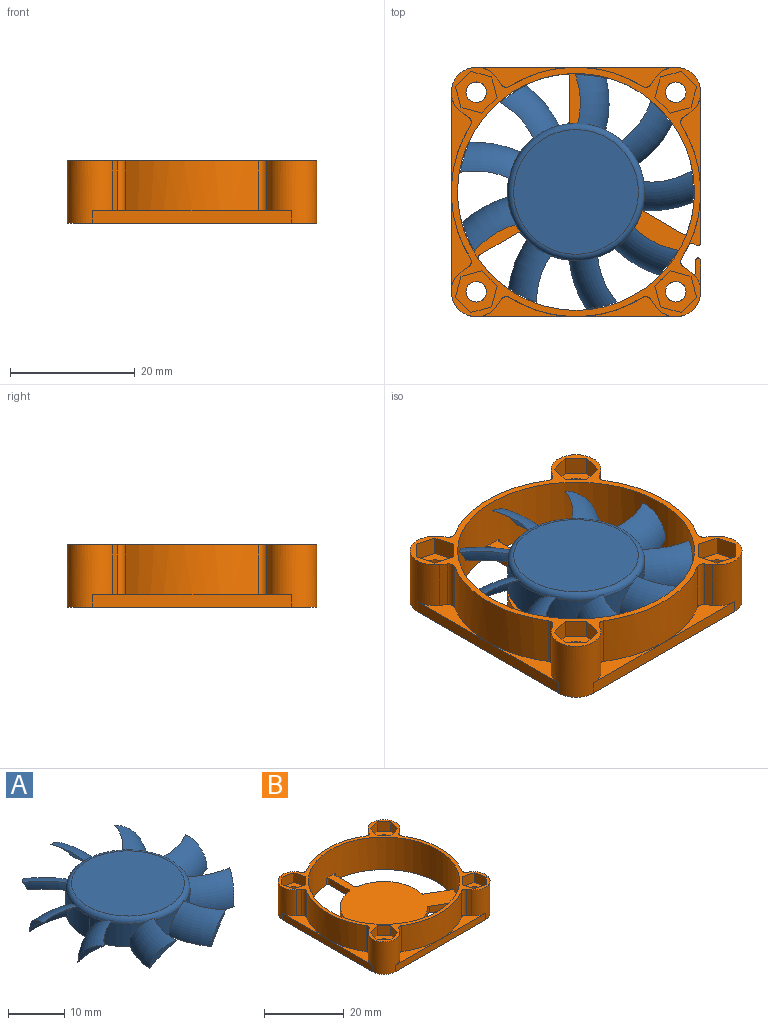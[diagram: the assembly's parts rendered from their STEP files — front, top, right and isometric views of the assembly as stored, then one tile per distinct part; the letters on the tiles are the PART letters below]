
ASSEMBLY  parts=2 mates=1
PART A: 32 faces, bbox 42.3x42.5x6 mm
  f0: cylinder r=11mm len=22mm, axis (0,0,-1), area 307.6mm2, adj f1,f3,f4,f5,f6,f8,f9,f11
  f1: cylinder r=11mm len=4.52mm, axis (0,0,-1), area 3.9mm2, adj f0,f4,f12
  f2: plane 20x20mm, normal (0,0,1), area 314.2mm2, adj f4
  f3: plane 22x22mm, normal (0,0,-1), area 380.1mm2, adj f0
  f4: torus R=10mm, axis (0,0,1), area 102.2mm2, adj f0,f1,f2,f5,f6,f8,f9,f11
  f5: torus R=5.4mm, axis (0,0,-1), area 55.4mm2, adj f0,f4,f6,f7
  f6: torus R=12.73mm, axis (0,0,-1), area 60.2mm2, adj f0,f4,f5,f7
  f7: cylinder r=18.8mm len=4.97mm, axis (0,0,1), area 4.5mm2, adj f5,f6
  f8: torus R=5.4mm, axis (0,0,-1), area 55.4mm2, adj f0,f4,f9,f10
  f9: torus R=12.73mm, axis (0,0,-1), area 60.2mm2, adj f0,f4,f8,f10
  f10: cylinder r=18.8mm len=4.97mm, axis (0,0,1), area 4.5mm2, adj f8,f9
  f11: torus R=5.4mm, axis (0,0,-1), area 55.4mm2, adj f0,f4,f12,f13
  f12: torus R=12.73mm, axis (0,0,-1), area 60.2mm2, adj f1,f4,f11,f13
  f13: cylinder r=18.8mm len=4.97mm, axis (0,0,1), area 4.5mm2, adj f11,f12
  f14: torus R=5.4mm, axis (0,0,-1), area 55.4mm2, adj f0,f4,f15,f16
  f15: torus R=12.73mm, axis (0,0,-1), area 60.2mm2, adj f0,f4,f14,f16
  f16: cylinder r=18.8mm len=4.97mm, axis (0,0,1), area 4.5mm2, adj f14,f15
  f17: torus R=5.4mm, axis (0,0,-1), area 55.4mm2, adj f0,f4,f18,f19
  f18: torus R=12.73mm, axis (0,0,-1), area 60.2mm2, adj f0,f4,f17,f19
  f19: cylinder r=18.8mm len=4.97mm, axis (0,0,1), area 4.5mm2, adj f17,f18
  f20: torus R=5.4mm, axis (0,0,-1), area 55.4mm2, adj f0,f4,f21,f22
  f21: torus R=12.73mm, axis (0,0,-1), area 60.2mm2, adj f0,f4,f20,f22
  f22: cylinder r=18.8mm len=4.99mm, axis (0,0,1), area 4.5mm2, adj f20,f21
  f23: torus R=5.4mm, axis (0,0,-1), area 55.4mm2, adj f0,f4,f24,f25
  f24: torus R=12.73mm, axis (0,0,-1), area 60.2mm2, adj f0,f4,f23,f25
  f25: cylinder r=18.8mm len=4.97mm, axis (0,0,1), area 4.5mm2, adj f23,f24
  f26: torus R=5.4mm, axis (0,0,-1), area 55.4mm2, adj f0,f4,f27,f28
  f27: torus R=12.73mm, axis (0,0,-1), area 60.2mm2, adj f0,f4,f26,f28
  f28: cylinder r=18.8mm len=5mm, axis (0,0,1), area 4.5mm2, adj f26,f27
  f29: torus R=5.4mm, axis (0,0,-1), area 55.4mm2, adj f0,f4,f30,f31
  f30: torus R=12.73mm, axis (0,0,-1), area 60.2mm2, adj f0,f4,f29,f31
  f31: cylinder r=18.8mm len=4.97mm, axis (0,0,1), area 4.5mm2, adj f29,f30
PART B: 115 faces, bbox 40x40x10 mm
  f0: plane 10.28x5.94mm, normal (0.5,0.87,0), area 11.9mm2, adj f19,f33,f35,f80,f81,f82
  f1: plane 2x1.78mm, normal (-1,0,0), area 3.6mm2, adj f8,f33,f81,f97
  f2: plane 16x3.21mm, normal (0,0,1), area 18mm2, adj f26,f27,f56,f57,f100
  f3: plane 16x3.21mm, normal (0,0,1), area 18mm2, adj f25,f26,f65,f69,f106
  f4: plane 16x3.21mm, normal (0,0,1), area 18mm2, adj f21,f22,f34,f60,f102
  f5: plane 16x3.21mm, normal (0,0,1), area 18mm2, adj f23,f24,f62,f63,f104
  f6: plane 16x3.21mm, normal (0,0,1), area 18mm2, adj f27,f28,f57,f58,f101
  f7: plane 35.04x31.24mm, normal (0,0,1), area 457.1mm2, adj f12,f13,f14,f15,f16,f17,f18,f30
  f8: plane 5.45x1.07mm, normal (0,0,1), area 3mm2, adj f1,f28,f29,f81,f96,f97
  f9: plane 16x3.21mm, normal (0,0,1), area 18mm2, adj f22,f23,f61,f62,f103
  f10: plane 8.58x1.89mm, normal (0,0,1), area 5.1mm2, adj f20,f21,f34,f76,f89
  f11: plane 16x3.21mm, normal (0,0,1), area 18mm2, adj f24,f25,f64,f65,f105
  f12: plane 7.04x2mm, normal (1,0,0), area 14.1mm2, adj f7,f33,f87,f92
  f13: cylinder r=19mm len=38mm, axis (0,0,1), area 1168mm2, adj f7,f33,f71,f83,f84,f85,f86,f87
  f14: plane 6.22x3.59mm, normal (0.5,0.87,0), area 14.4mm2, adj f7,f33,f88,f95
  f15: plane 6.09x3.52mm, normal (0.5,-0.87,0), area 14.1mm2, adj f7,f33,f84,f90
  f16: cylinder r=11mm len=16.31mm, axis (0,0,1), area 36.9mm2, adj f7,f33,f90,f94
  f17: plane 6.09x3.52mm, normal (-0.5,0.87,0), area 14.1mm2, adj f7,f33,f85,f91
  f18: plane 7.04x2mm, normal (-1,0,0), area 14.1mm2, adj f7,f33,f86,f93
  f19: cylinder r=11mm len=3.9mm, axis (0,0,1), area 4.4mm2, adj f0,f20,f33,f35,f77
  f20: plane 8.8x5.08mm, normal (-0.5,-0.87,0), area 6.1mm2, adj f10,f19,f33,f76,f77,f78,f89
  f21: plane 24.08x2mm, normal (1,0,0), area 48.2mm2, adj f4,f10,f22,f33,f89
  f22: cylinder r=4mm len=10mm, axis (0,0,1), area 124.5mm2, adj f4,f9,f21,f23,f33,f60,f61,f71
  f23: plane 32x2mm, normal (0,1,0), area 64mm2, adj f5,f9,f22,f24,f33
  f24: cylinder r=4mm len=10mm, axis (0,0,1), area 124.5mm2, adj f5,f11,f23,f25,f33,f63,f64,f71
  f25: plane 32x2mm, normal (-1,0,0), area 64mm2, adj f3,f11,f24,f26,f33
  f26: cylinder r=4mm len=10mm, axis (0,0,1), area 124.5mm2, adj f2,f3,f25,f27,f33,f56,f69,f71
  f27: plane 32x2mm, normal (0,-1,0), area 64mm2, adj f2,f6,f26,f28,f33
  f28: cylinder r=4mm len=10mm, axis (0,0,1), area 124.9mm2, adj f6,f8,f27,f29,f33,f58,f59,f71
  f29: plane 4.96x2mm, normal (1,0,0), area 9.9mm2, adj f8,f28,f33,f96
  f30: plane 6.22x3.59mm, normal (-0.5,-0.87,0), area 14.4mm2, adj f7,f33,f83,f94
  f31: cylinder r=11mm len=15.12mm, axis (0,0,1), area 40.3mm2, adj f7,f33,f91,f93
  f32: cylinder r=11mm len=13.49mm, axis (0,0,1), area 36.9mm2, adj f7,f33,f92,f95
  f33: plane 40x40mm, normal (0,0,-1), area 793.4mm2, adj f0,f1,f12,f13,f14,f15,f16,f17
  f34: cylinder r=20mm len=21.25mm, axis (0,0,1), area 180.4mm2, adj f4,f10,f71,f76,f79,f98,f102
  f35: plane 9.49x8.4mm, normal (0,0,-1), area 34.2mm2, adj f0,f19,f77,f79,f80
  f36: plane 3.35x3mm, normal (-0.26,-0.97,0), area 10.4mm2, adj f37,f70,f71,f75
  f37: plane 3.35x3mm, normal (-0.97,-0.26,0), area 10.4mm2, adj f36,f38,f71,f75
  f38: plane 3x2.45mm, normal (-0.71,0.71,0), area 10.4mm2, adj f37,f39,f71,f75
  f39: plane 3.35x3mm, normal (0.26,0.97,0), area 10.4mm2, adj f38,f40,f71,f75
  f40: plane 3.35x3mm, normal (0.97,0.26,0), area 10.4mm2, adj f39,f70,f71,f75
  f41: plane 3x2.45mm, normal (-0.71,0.71,0), area 10.4mm2, adj f42,f66,f71,f73
  f42: plane 3.35x3mm, normal (0.26,0.97,0), area 10.4mm2, adj f41,f43,f71,f73
  f43: plane 3.35x3mm, normal (0.97,0.26,0), area 10.4mm2, adj f42,f44,f71,f73
  f44: plane 3x2.45mm, normal (0.71,-0.71,0), area 10.4mm2, adj f43,f45,f71,f73
  f45: plane 3.35x3mm, normal (-0.26,-0.97,0), area 10.4mm2, adj f44,f66,f71,f73
  f46: plane 3.35x3mm, normal (-0.97,0.26,0), area 10.4mm2, adj f47,f67,f71,f72
  f47: plane 3.35x3mm, normal (-0.26,0.97,0), area 10.4mm2, adj f46,f48,f71,f72
  f48: plane 3x2.45mm, normal (0.71,0.71,0), area 10.4mm2, adj f47,f49,f71,f72
  f49: plane 3.35x3mm, normal (0.97,-0.26,0), area 10.4mm2, adj f48,f50,f71,f72
  f50: plane 3.35x3mm, normal (0.26,-0.97,0), area 10.4mm2, adj f49,f67,f71,f72
  f51: plane 3x2.45mm, normal (-0.71,-0.71,0), area 10.4mm2, adj f52,f68,f71,f74
  f52: plane 3.35x3mm, normal (-0.97,0.26,0), area 10.4mm2, adj f51,f53,f71,f74
  f53: plane 3.35x3mm, normal (-0.26,0.97,0), area 10.4mm2, adj f52,f54,f71,f74
  f54: plane 3x2.45mm, normal (0.71,0.71,0), area 10.4mm2, adj f53,f55,f71,f74
  f55: plane 3.35x3mm, normal (0.97,-0.26,0), area 10.4mm2, adj f54,f68,f71,f74
  f56: plane 8x1.06mm, normal (0.82,-0.57,0), area 10.4mm2, adj f2,f26,f71,f100
  f57: cylinder r=20mm len=21.25mm, axis (0,0,-1), area 179.2mm2, adj f2,f6,f71,f100,f101
  f58: plane 8x1.06mm, normal (-0.82,-0.57,0), area 10.4mm2, adj f6,f28,f71,f101
  f59: plane 8.5x1.06mm, normal (0.57,0.82,0), area 11mm2, adj f28,f71,f80,f98
  f60: plane 8x1.06mm, normal (0.57,-0.82,0), area 10.4mm2, adj f4,f22,f71,f102
  f61: plane 8x1.06mm, normal (-0.82,0.57,0), area 10.4mm2, adj f9,f22,f71,f103
  f62: cylinder r=20mm len=21.25mm, axis (0,0,-1), area 179.2mm2, adj f5,f9,f71,f103,f104
  f63: plane 8x1.06mm, normal (0.82,0.57,0), area 10.4mm2, adj f5,f24,f71,f104
  f64: plane 8x1.06mm, normal (-0.57,-0.82,0), area 10.4mm2, adj f11,f24,f71,f105
  f65: cylinder r=20mm len=21.25mm, axis (0,0,-1), area 179.2mm2, adj f3,f11,f71,f105,f106
  f66: plane 3.35x3mm, normal (-0.97,-0.26,0), area 10.4mm2, adj f41,f45,f71,f73
  f67: plane 3x2.45mm, normal (-0.71,-0.71,0), area 10.4mm2, adj f46,f50,f71,f72
  f68: plane 3.35x3mm, normal (0.26,-0.97,0), area 10.4mm2, adj f51,f55,f71,f74
  f69: plane 8x1.06mm, normal (-0.57,0.82,0), area 10.4mm2, adj f3,f26,f71,f106
  f70: plane 3x2.45mm, normal (0.71,-0.71,0), area 10.4mm2, adj f36,f40,f71,f75
  f71: plane 40x40mm, normal (0,0,1), area 183.3mm2, adj f13,f22,f24,f26,f28,f34,f36,f37
  f72: plane 6.69x6.69mm, normal (0,0,1), area 22.6mm2, adj f46,f47,f48,f49,f50,f67,f111
  f73: plane 6.69x6.69mm, normal (0,0,1), area 22.6mm2, adj f41,f42,f43,f44,f45,f66,f109
  f74: plane 6.69x6.69mm, normal (0,0,1), area 22.6mm2, adj f51,f52,f53,f54,f55,f68,f107
  f75: plane 6.69x6.69mm, normal (0,0,1), area 22.6mm2, adj f36,f37,f38,f39,f40,f70,f113
  f76: cylinder r=0.5mm len=0.7mm, axis (0,0,1), area 0.4mm2, adj f10,f20,f34,f78
  f77: cylinder r=0.5mm len=7.74mm, axis (0.87,-0.5,0), area 6.8mm2, adj f19,f20,f35,f78
  f78: bspline ~1.22x1.19mm, area 0.9mm2, adj f20,f76,f77,f79
  f79: torus R=19.5mm, axis (0,0,1), area 2.5mm2, adj f34,f35,f78,f99
  f80: cylinder r=0.5mm len=2.57mm, axis (0.82,-0.57,0), area 1.5mm2, adj f0,f35,f59,f82,f99
  f81: cylinder r=0.5mm len=2mm, axis (0,0,-1), area 1.7mm2, adj f0,f1,f8,f28,f33,f82
  f82: torus R=3.5mm, axis (0,0,1), area 0.4mm2, adj f0,f28,f80,f81
  f83: cylinder r=0.5mm len=2mm, axis (0,0,1), area 1.7mm2, adj f7,f13,f30,f33
  f84: cylinder r=0.5mm len=2mm, axis (0,0,1), area 1.7mm2, adj f7,f13,f15,f33
  f85: cylinder r=0.5mm len=2mm, axis (0,0,1), area 1.7mm2, adj f7,f13,f17,f33
  f86: cylinder r=0.5mm len=2mm, axis (0,0,1), area 1.7mm2, adj f7,f13,f18,f33
  f87: cylinder r=0.5mm len=2mm, axis (0,0,1), area 1.7mm2, adj f7,f12,f13,f33
  f88: cylinder r=0.5mm len=2mm, axis (0,0,1), area 1.7mm2, adj f7,f13,f14,f33
  f89: cylinder r=0.5mm len=2mm, axis (0,0,-1), area 2.1mm2, adj f10,f20,f21,f33
  f90: cylinder r=0.5mm len=2mm, axis (0,0,1), area 1.4mm2, adj f7,f15,f16,f33
  f91: cylinder r=0.5mm len=2mm, axis (0,0,1), area 1.4mm2, adj f7,f17,f31,f33
  f92: cylinder r=0.5mm len=2mm, axis (0,0,1), area 1.4mm2, adj f7,f12,f32,f33
  f93: cylinder r=0.5mm len=2mm, axis (0,0,1), area 1.4mm2, adj f7,f18,f31,f33
  f94: cylinder r=0.5mm len=2mm, axis (0,0,1), area 1.3mm2, adj f7,f16,f30,f33
  f95: cylinder r=0.5mm len=2mm, axis (0,0,1), area 1.3mm2, adj f7,f14,f32,f33
  f96: cylinder r=0.5mm len=2mm, axis (0,0,1), area 1.4mm2, adj f8,f29,f33,f97
  f97: cylinder r=0.5mm len=2mm, axis (0,0,1), area 1.4mm2, adj f1,f8,f33,f96
  f98: cylinder r=1mm len=8.5mm, axis (0,0,1), area 12.9mm2, adj f34,f59,f71,f99
  f99: bspline ~1.5x1.35mm, area 0.5mm2, adj f79,f80,f98
  f100: cylinder r=1mm len=8mm, axis (0,0,-1), area 12.2mm2, adj f2,f56,f57,f71
  f101: cylinder r=1mm len=8mm, axis (0,0,-1), area 12.2mm2, adj f6,f57,f58,f71
  f102: cylinder r=1mm len=8mm, axis (0,0,1), area 12.2mm2, adj f4,f34,f60,f71
  f103: cylinder r=1mm len=8mm, axis (0,0,-1), area 12.2mm2, adj f9,f61,f62,f71
  f104: cylinder r=1mm len=8mm, axis (0,0,-1), area 12.2mm2, adj f5,f62,f63,f71
  f105: cylinder r=1mm len=8mm, axis (0,0,-1), area 12.2mm2, adj f11,f64,f65,f71
  f106: cylinder r=1mm len=8mm, axis (0,0,-1), area 12.2mm2, adj f3,f65,f69,f71
  f107: cylinder r=1.65mm len=6.4mm, axis (0,0,-1), area 66.4mm2, adj f74,f108
  f108: cone r=1.65mm half-angle=45deg, axis (0,0,-1), area 10.4mm2, adj f33,f107
  f109: cylinder r=1.65mm len=6.4mm, axis (0,0,-1), area 66.4mm2, adj f73,f110
  f110: cone r=1.65mm half-angle=45deg, axis (0,0,-1), area 10.4mm2, adj f33,f109
  f111: cylinder r=1.65mm len=6.4mm, axis (0,0,-1), area 66.4mm2, adj f72,f112
  f112: cone r=1.65mm half-angle=45deg, axis (0,0,-1), area 10.4mm2, adj f33,f111
  f113: cylinder r=1.65mm len=6.4mm, axis (0,0,-1), area 66.4mm2, adj f75,f114
  f114: cone r=1.65mm half-angle=45deg, axis (0,0,-1), area 10.4mm2, adj f33,f113
PLACE A rot(axis=(0,0,-1),81.8deg) t=(0,0,0)mm
PLACE B at identity fixed
MATE revolute A.f0 <-> B.f13  axis (0,0,-1) through (0,0,0)mm
